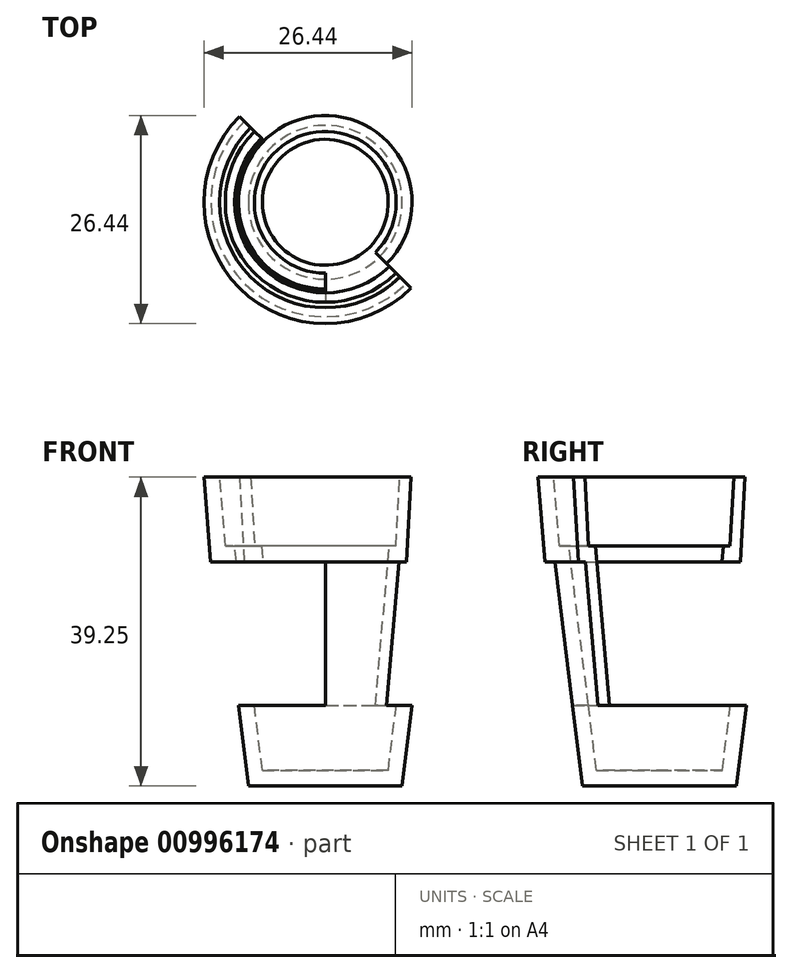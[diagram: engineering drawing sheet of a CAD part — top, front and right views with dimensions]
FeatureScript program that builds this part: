
annotation { "Feature Type Name" : "Feature", "Feature Type Description" : "" }
export const myFeature = defineFeature(function(context is Context, id is Id, definition is map)
    precondition{}
    {
        {
            var Q0;
            Q0=qCreatedBy(makeId("Front.planeOp"),FACE);
            var sketch = newSketch(context, id + "F0", { "sketchPlane" : qUnion([Q0])});
            skLineSegment(sketch, "E0", {"start": v(0, 0) * mm, "end": v(8, 0) * mm});
            skLineSegment(sketch, "E1", {"start": v(0, 0) * mm, "end": v(0, 28.5) * mm, "construction": true});
            skLineSegment(sketch, "E2", {"start": v(0, 28.5) * mm, "end": v(11.5, 28.5) * mm, "construction": true});
            skLineSegment(sketch, "E3", {"start": v(11.5, 28.5) * mm, "end": v(8, 0) * mm});
            skLineSegment(sketch, "E4", {"start": v(0, -2) * mm, "end": v(0, 0) * mm});
            skLineSegment(sketch, "E5", {"start": v(0, 28.5) * mm, "end": v(0, 37.25) * mm, "construction": true});
            skLineSegment(sketch, "E6", {"start": v(12.7, 28.5) * mm, "end": v(13.4, 37.25) * mm});
            skLineSegment(sketch, "E7", {"start": v(11.5, 28.5) * mm, "end": v(12.7, 28.5) * mm});
            skLineSegment(sketch, "E8.0", {"start": v(14.55, 26.5) * mm, "end": v(15.4, 37.25) * mm});
            skLineSegment(sketch, "E8.1", {"start": v(13.27, 26.5) * mm, "end": v(14.55, 26.5) * mm});
            skLineSegment(sketch, "E8.2", {"start": v(13.27, 26.5) * mm, "end": v(9.77, -2) * mm});
            skLineSegment(sketch, "E8.3", {"start": v(0, -2) * mm, "end": v(9.77, -2) * mm});
            skLineSegment(sketch, "E9", {"start": v(0, 37.25) * mm, "end": v(29.09, 37.25) * mm, "construction": true});
            skLineSegment(sketch, "E10", {"start": v(13.4, 37.25) * mm, "end": v(15.4, 37.25) * mm});
            skSolve(sketch);
        }
        {
            var Q0;
            Q0 = qSketchRegion(id + "F0", true);
            var Q1;
            Q1=sQuery(id+"F0.wireOp",EDGE,"E1");
            revolve(context, id + "F1", {"surfaceOperationType" : NewSurfaceOperationType.NEW, "entities" : qUnion([Q0]), "axis" : qUnion([Q1]), "revolveType" : RevolveType.FULL});
        }
        {
            var Q0;
            Q0=makeQuery(id+"F1.opRevolve","SWEPT_FACE",FACE,{"disambiguationData":[OSD([sQuery(id+"F0.wireOp",EDGE,"E8.1")])]});
            var sketch = newSketch(context, id + "F2", { "sketchPlane" : qUnion([Q0])});
            skLineSegment(sketch, "E11.bottom", {"start": v(-20.1, 0) * mm, "end": v(20.3, 0) * mm});
            skLineSegment(sketch, "E11.top", {"start": v(-20.1, -19.12) * mm, "end": v(20.3, -19.12) * mm});
            skLineSegment(sketch, "E11.left", {"start": v(-20.1, 0) * mm, "end": v(-20.1, -19.12) * mm});
            skLineSegment(sketch, "E11.right", {"start": v(20.3, 0) * mm, "end": v(20.3, -19.12) * mm});
            skLineSegment(sketch, "E12.bottom", {"start": v(0, 0) * mm, "end": v(-21.1, 0) * mm});
            skLineSegment(sketch, "E12.top", {"start": v(0, 20.2) * mm, "end": v(-21.1, 20.2) * mm});
            skLineSegment(sketch, "E12.left", {"start": v(0, 0) * mm, "end": v(0, 20.2) * mm});
            skLineSegment(sketch, "E12.right", {"start": v(-21.1, 0) * mm, "end": v(-21.1, 20.2) * mm});
            skSolve(sketch);
        }
        {
            var Q0;
            Q0 = qSketchRegion(id + "F2", true);
            extrude(context, id + "F3", {"entities" : qUnion([Q0]), "operationType" : NewBodyOperationType.REMOVE, "depth" : 18.25 * mm, "offsetDistance" : 25 * mm});
        }
        {
            var Q0;
            Q0=makeQuery(id+"F1.opRevolve","SWEPT_FACE",FACE,{"disambiguationData":[OSD([sQuery(id+"F0.wireOp",EDGE,"E10")])]});
            var sketch = newSketch(context, id + "F4", { "sketchPlane" : qUnion([Q0])});
            skLineSegment(sketch, "E13", {"start": v(-39.03, 0) * mm, "end": v(43.39, 0) * mm, "construction": true});
            skLineSegment(sketch, "E14", {"start": v(-31.6, 31.6) * mm, "end": v(25.36, -25.36) * mm});
            skLineSegment(sketch, "E15", {"start": v(-31.6, 31.6) * mm, "end": v(25.36, 31.6) * mm});
            skLineSegment(sketch, "E16", {"start": v(25.36, 31.6) * mm, "end": v(25.36, -25.36) * mm});
            skSolve(sketch);
        }
        {
            var Q0;
            Q0 = qSketchRegion(id + "F4", true);
            extrude(context, id + "F5", {"entities" : qUnion([Q0]), "operationType" : NewBodyOperationType.REMOVE, "oppositeDirection" : true, "depth" : 29 * mm, "offsetDistance" : 25 * mm});
        }
    });
